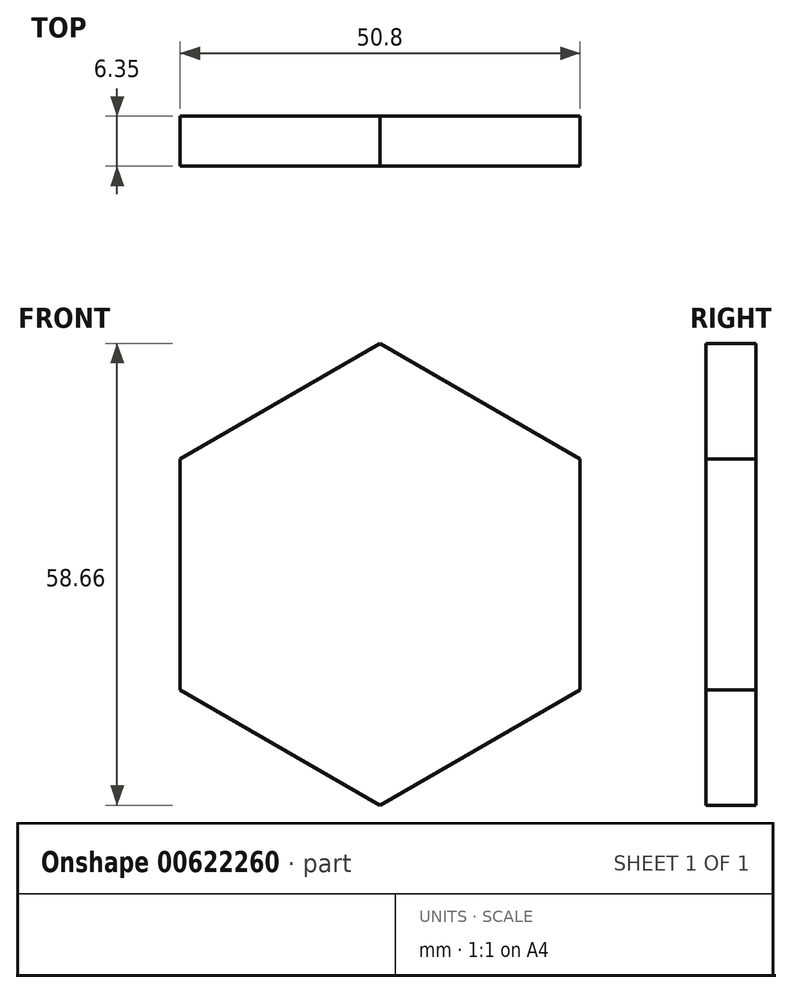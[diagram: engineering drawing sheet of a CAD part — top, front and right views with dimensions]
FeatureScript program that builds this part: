
annotation { "Feature Type Name" : "Feature", "Feature Type Description" : "" }
export const myFeature = defineFeature(function(context is Context, id is Id, definition is map)
    precondition{}
    {
        {
            var Q0;
            Q0=qCreatedBy(makeId("Front.planeOp"),FACE);
            var sketch = newSketch(context, id + "F0", { "sketchPlane" : qUnion([Q0])});
            skCircle(sketch, "E0.cCircle", {"center": v(0, 0) * mm, "radius": 25.4 * mm, "construction": true});
            skLineSegment(sketch, "E0.0", {"start": v(25.4, 14.66) * mm, "end": v(25.4, -14.66) * mm});
            skLineSegment(sketch, "E0.1", {"start": v(25.4, -14.66) * mm, "end": v(0, -29.33) * mm});
            skLineSegment(sketch, "E0.2", {"start": v(0, -29.33) * mm, "end": v(-25.4, -14.66) * mm});
            skLineSegment(sketch, "E0.3", {"start": v(-25.4, -14.66) * mm, "end": v(-25.4, 14.66) * mm});
            skLineSegment(sketch, "E0.4", {"start": v(-25.4, 14.66) * mm, "end": v(0, 29.33) * mm});
            skLineSegment(sketch, "E0.5", {"start": v(0, 29.33) * mm, "end": v(25.4, 14.66) * mm});
            skPoint(sketch, "E0.0.midPoint", {"position": v(25.4, 0) * mm});
            skSolve(sketch);
        }
        {
            var Q0;
            Q0=makeQuery(id+"F0.imprint","IMPRINT",FACE,{"disambiguationData":[TD([[makeQuery(id+"F0.imprint","IMPRINT",EDGE,{"derivedFrom":sQuery(id+"F0.wireOp",EDGE,"E0.0")}),-1.0]])]});
            extrude(context, id + "F1", {"entities" : qUnion([Q0]), "depth" : 6.35 * mm, "offsetDistance" : 25.4 * mm});
        }
    });
